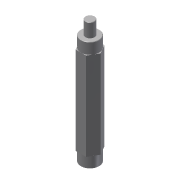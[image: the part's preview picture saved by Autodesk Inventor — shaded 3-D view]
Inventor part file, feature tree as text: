
AUTODESK INVENTOR PART (.ipt)
format: ipt  version: 2013 (Build 170138000, 138)  size: 101,888 bytes
history: native  units: in
note: dims shown in document units (in); Inventor stores cm internally (conversion verified against a paired STEP export)
features: chamfer x1, other x1, imported_body x1
ambient origin geometry x8: Origin, YZ Plane, XZ Plane, XY Plane, X Axis, Y Axis, Z Axis, Center Point
feature tree (3):
  chamfer  "Chamfer4"  [1 undecoded]
  other  "446 Cluster Hex Shaft 5001"
  imported_body  "Base1"
note: 1 required parameter value undecoded (feature->parameter linkage not recoverable at this tier; creation-order binding heuristic only, values carry confidence <= 0.55)
